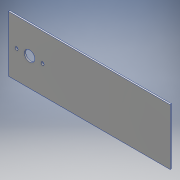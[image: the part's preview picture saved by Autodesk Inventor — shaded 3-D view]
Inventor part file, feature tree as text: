
AUTODESK INVENTOR PART (.ipt)
format: ipt  version: 2016 (Build 200138000, 138)  size: 115,712 bytes
history: native  units: mm
features: extrude x2, sketch x2, other x1
ambient origin geometry x8: Origin, YZ Plane, XZ Plane, XY Plane, X Axis, Y Axis, Z Axis, Center Point
bodies: Body1 (feature_tree)
feature tree (5):
  other  "ソリッド1"
  extrude  "押し出し1"  Depth=230.0mm
  extrude  "押し出し2"  Depth=80.0mm
  sketch  "スケッチ1"
  sketch  "スケッチ2"
